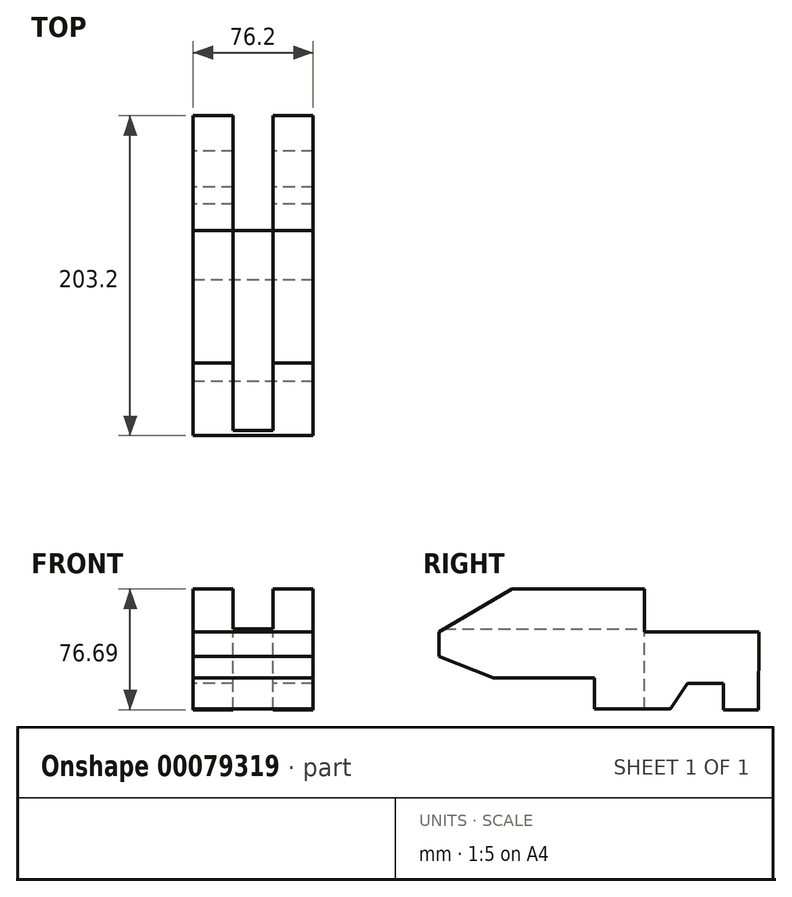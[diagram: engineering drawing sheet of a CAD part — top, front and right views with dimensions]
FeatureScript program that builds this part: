
annotation { "Feature Type Name" : "Feature", "Feature Type Description" : "" }
export const myFeature = defineFeature(function(context is Context, id is Id, definition is map)
    precondition{}
    {
        {
            var Q0;
            Q0=qCreatedBy(makeId("Right.planeOp"),FACE);
            var sketch = newSketch(context, id + "F0", { "sketchPlane" : qUnion([Q0])});
            skLineSegment(sketch, "E0", {"start": v(72.92, 0) * mm, "end": v(0, 0) * mm});
            skLineSegment(sketch, "E1", {"start": v(0, 0) * mm, "end": v(0, 27.28) * mm});
            skLineSegment(sketch, "E2", {"start": v(0, 27.28) * mm, "end": v(-84.07, 27.28) * mm});
            skLineSegment(sketch, "E3", {"start": v(-84.07, 27.28) * mm, "end": v(-130.28, 0) * mm});
            skLineSegment(sketch, "E4", {"start": v(-130.28, 0) * mm, "end": v(-130.28, -15.49) * mm});
            skLineSegment(sketch, "E5", {"start": v(-130.28, -15.49) * mm, "end": v(-95.86, -29.25) * mm});
            skLineSegment(sketch, "E6", {"start": v(-95.86, -29.25) * mm, "end": v(-31.46, -29.25) * mm});
            skLineSegment(sketch, "E7", {"start": v(-31.46, -29.25) * mm, "end": v(-31.46, -48.92) * mm});
            skLineSegment(sketch, "E8", {"start": v(-31.46, -48.92) * mm, "end": v(0, -48.92) * mm});
            skLineSegment(sketch, "E9", {"start": v(0, -48.92) * mm, "end": v(16.71, -48.92) * mm});
            skLineSegment(sketch, "E10", {"start": v(16.71, -48.92) * mm, "end": v(27.53, -32.7) * mm});
            skLineSegment(sketch, "E11", {"start": v(27.53, -32.7) * mm, "end": v(50.3, -32.7) * mm});
            skLineSegment(sketch, "E12", {"start": v(50.3, -32.7) * mm, "end": v(50.3, -49.4) * mm});
            skLineSegment(sketch, "E13", {"start": v(50.3, -49.4) * mm, "end": v(72.43, -49.4) * mm});
            skLineSegment(sketch, "E14", {"start": v(72.43, -49.4) * mm, "end": v(72.92, 0) * mm});
            skSolve(sketch);
        }
        {
            var Q0;
            Q0 = qSketchRegion(id + "F0", true);
            extrude(context, id + "F1", {"entities" : qUnion([Q0]), "depth" : 76.2 * mm});
        }
        {
            var Q0;
            Q0=makeQuery(id+"F1.opExtrude","SWEPT_FACE",FACE,{"disambiguationData":[OSD([sQuery(id+"F0.wireOp",EDGE,"E2")])]});
            var sketch = newSketch(context, id + "F2", { "sketchPlane" : qUnion([Q0])});
            skLineSegment(sketch, "E15", {"start": v(25.4, 0) * mm, "end": v(25.4, 73.63) * mm});
            skLineSegment(sketch, "E16", {"start": v(25.4, 73.63) * mm, "end": v(50.8, 73.63) * mm});
            skLineSegment(sketch, "E17", {"start": v(50.8, 73.63) * mm, "end": v(50.8, 0) * mm});
            skLineSegment(sketch, "E18", {"start": v(25.4, 0) * mm, "end": v(25.4, -129.52) * mm});
            skLineSegment(sketch, "E19", {"start": v(25.4, -129.52) * mm, "end": v(50.8, -129.52) * mm});
            skLineSegment(sketch, "E20", {"start": v(50.8, -129.52) * mm, "end": v(50.8, 0) * mm});
            skSolve(sketch);
        }
        {
            var Q0;
            Q0 = qSketchRegion(id + "F2", true);
            extrude(context, id + "F3", {"entities" : qUnion([Q0]), "operationType" : NewBodyOperationType.REMOVE, "oppositeDirection" : true, "depth" : 25.4 * mm});
        }
        {
            var Q0;
            Q0=makeQuery(id+"F1.opExtrude","SWEPT_FACE",FACE,{"disambiguationData":[OSD([sQuery(id+"F0.wireOp",EDGE,"E0")])]});
            var sketch = newSketch(context, id + "F4", { "sketchPlane" : qUnion([Q0])});
            skLineSegment(sketch, "E21", {"start": v(50.8, 0) * mm, "end": v(50.8, 72.92) * mm});
            skLineSegment(sketch, "E22", {"start": v(25.4, 0) * mm, "end": v(25.4, 72.92) * mm});
            skSolve(sketch);
        }
        {
            var Q0;
            {var subQ0=sQuery(id+"F4.wireOp",EDGE,"E21");Q0=makeQuery(id+"F4.imprint","IMPRINT",FACE,{"disambiguationData":[TD([[makeQuery(id+"F4.imprint","IMPRINT",EDGE,{"derivedFrom":subQ0}),1.0]])]});}
            extrude(context, id + "F5", {"entities" : qUnion([Q0]), "operationType" : NewBodyOperationType.REMOVE, "oppositeDirection" : true, "depth" : 50.8 * mm});
        }
    });
